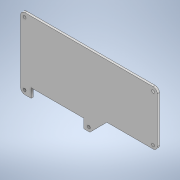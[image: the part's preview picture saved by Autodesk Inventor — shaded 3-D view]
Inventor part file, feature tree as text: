
AUTODESK INVENTOR PART (.ipt)
format: ipt  version: 2021 (Build 250183000, 183)  size: 140,288 bytes
history: native  units: mm
features: sketch x3, extrude x2, hole x1, fillet x1
ambient origin geometry x8: Origin, YZ Plane, XZ Plane, XY Plane, X Axis, Y Axis, Z Axis, Center Point
bodies: Solid1 (feature_tree)
feature tree (7):
  extrude  "Extrusion1"  Depth=52.0mm
  hole  "Hole1"  [1 undecoded]
  extrude  "Extrusion2"  Depth=3.0mm
  fillet  "Fillet1"  Radius=3.0mm
  sketch  "Sketch1"  dims[d0=100.0mm d1=52.0mm]
  sketch  "Sketch2"  dims[d2=50.0mm d3=26.0mm]
  sketch  "Sketch3"  dims[d4=1.6mm d5=0.0mm d6=3.0mm d7=3.0mm d8=50.0mm d9=3.0mm d10=97.0mm d11=15.0mm d12=3.0mm d13=49.0mm d14=97.0mm d15=49.0mm d16=2.1mm d17=6.0mm d18=4.0mm d19=2.0mm d20=90.0deg d21=10.0mm d22=20.594885mm d23=7.7mm d24=6.7mm d25=46.4mm d26=50.7mm d27=63.1mm d28=12.5mm d29=1.6mm d30=0.0mm d31=3.0mm]
note: 1 required parameter value undecoded (feature->parameter linkage not recoverable at this tier; creation-order binding heuristic only, values carry confidence <= 0.55)
